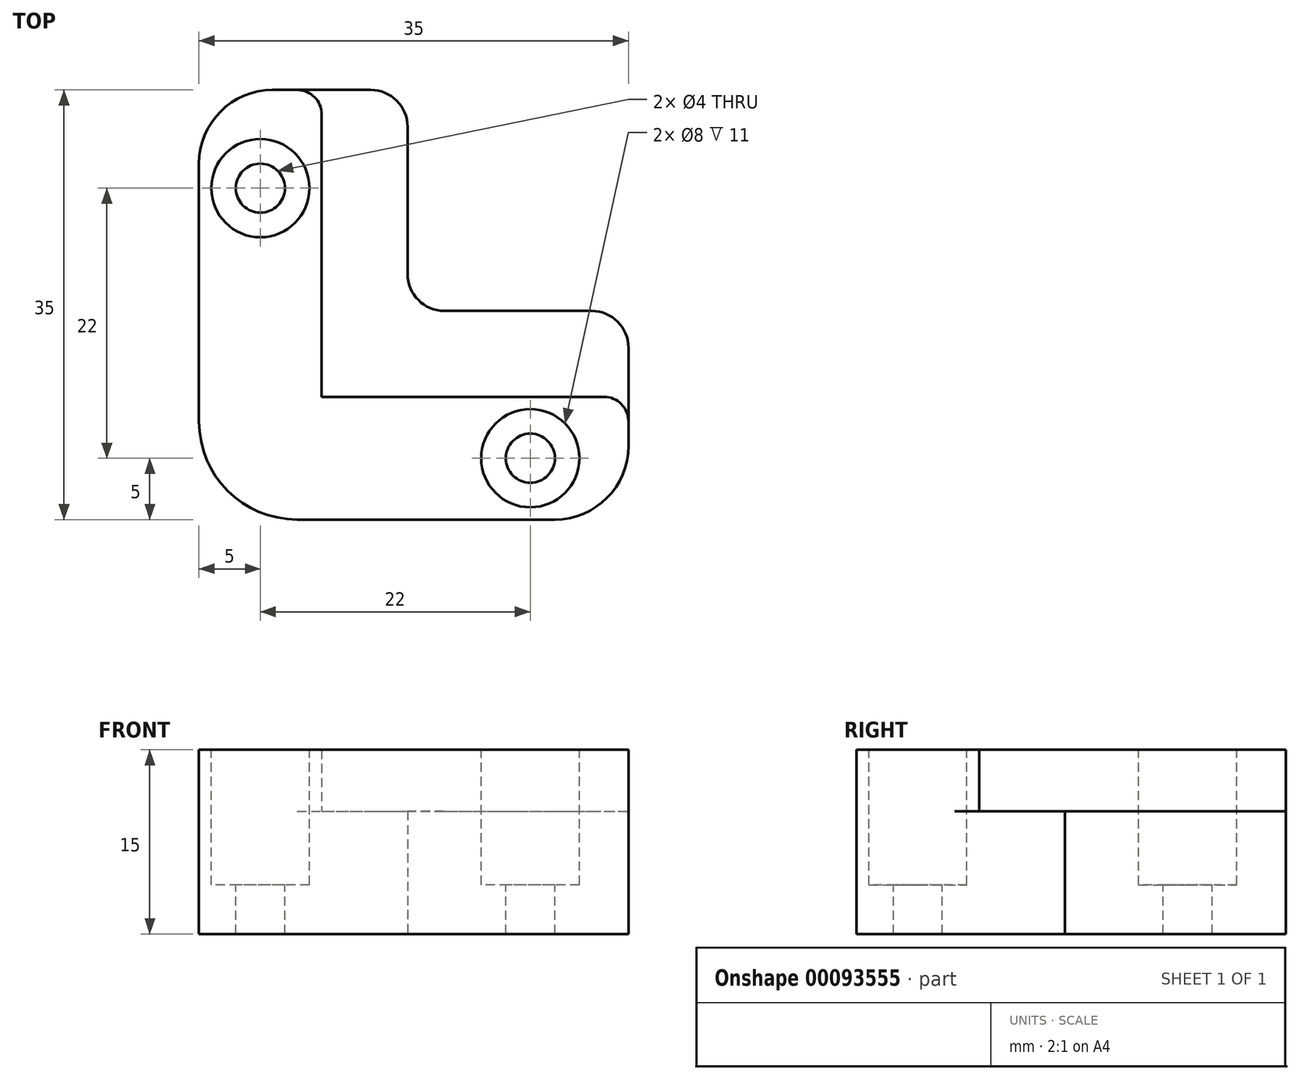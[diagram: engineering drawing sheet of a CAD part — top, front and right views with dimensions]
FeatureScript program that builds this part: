
annotation { "Feature Type Name" : "Feature", "Feature Type Description" : "" }
export const myFeature = defineFeature(function(context is Context, id is Id, definition is map)
    precondition{}
    {
        {
            var Q0;
            Q0=qCreatedBy(makeId("Top.planeOp"),FACE);
            var sketch = newSketch(context, id + "F0", { "sketchPlane" : qUnion([Q0])});
            skLineSegment(sketch, "E0", {"start": v(0, 0) * mm, "end": v(25, 0) * mm});
            skLineSegment(sketch, "E1", {"start": v(25, 0) * mm, "end": v(25, -10) * mm});
            skLineSegment(sketch, "E2", {"start": v(25, -10) * mm, "end": v(-10, -10) * mm});
            skLineSegment(sketch, "E3", {"start": v(-10, -10) * mm, "end": v(-10, 25) * mm});
            skLineSegment(sketch, "E4", {"start": v(-10, 25) * mm, "end": v(0, 25) * mm});
            skLineSegment(sketch, "E5", {"start": v(0, 25) * mm, "end": v(0, 0) * mm});
            skSolve(sketch);
        }
        {
            var Q0;
            Q0 = qSketchRegion(id + "F0", true);
            extrude(context, id + "F1", {"entities" : qUnion([Q0]), "depth" : 15 * mm});
        }
        {
            var Q0;
            Q0=makeQuery(id+"F1.opExtrude","CAP_FACE",FACE,{"disambiguationData":[OSD([sQuery(id+"F0.wireOp",EDGE,"E0"),sQuery(id+"F0.wireOp",EDGE,"E1"),sQuery(id+"F0.wireOp",EDGE,"E2"),sQuery(id+"F0.wireOp",EDGE,"E3"),sQuery(id+"F0.wireOp",EDGE,"E4"),sQuery(id+"F0.wireOp",EDGE,"E5")])],"isStart":true});
            var sketch = newSketch(context, id + "F2", { "sketchPlane" : qUnion([Q0])});
            skLineSegment(sketch, "E6", {"start": v(0, 0) * mm, "end": v(0, -25) * mm});
            skLineSegment(sketch, "E7", {"start": v(0, -25) * mm, "end": v(7, -25) * mm});
            skLineSegment(sketch, "E8", {"start": v(7, -25) * mm, "end": v(7, -7) * mm});
            skLineSegment(sketch, "E9", {"start": v(7, -7) * mm, "end": v(25, -7) * mm});
            skLineSegment(sketch, "E10", {"start": v(25, -7) * mm, "end": v(25, 0) * mm});
            skLineSegment(sketch, "E11", {"start": v(25, 0) * mm, "end": v(0, 0) * mm});
            skSolve(sketch);
        }
        {
            var Q0;
            Q0 = qSketchRegion(id + "F2", true);
            extrude(context, id + "F3", {"entities" : qUnion([Q0]), "operationType" : NewBodyOperationType.ADD, "oppositeDirection" : true, "depth" : 10 * mm});
        }
        {
            var Q0;
            Q0=makeQuery(id+"F1.opExtrude","CAP_FACE",FACE,{"disambiguationData":[OSD([sQuery(id+"F0.wireOp",EDGE,"E0"),sQuery(id+"F0.wireOp",EDGE,"E1"),sQuery(id+"F0.wireOp",EDGE,"E2"),sQuery(id+"F0.wireOp",EDGE,"E3"),sQuery(id+"F0.wireOp",EDGE,"E4"),sQuery(id+"F0.wireOp",EDGE,"E5")])],"isStart":false});
            var sketch = newSketch(context, id + "F4", { "sketchPlane" : qUnion([Q0])});
            skLineSegment(sketch, "E12", {"start": v(25, -5) * mm, "end": v(-10, -5) * mm, "construction": true});
            skLineSegment(sketch, "E13", {"start": v(-5, 25) * mm, "end": v(-5, -10) * mm, "construction": true});
            skCircle(sketch, "E14", {"center": v(17, -5) * mm, "radius": 2 * mm});
            skCircle(sketch, "E15", {"center": v(-5, 17) * mm, "radius": 2 * mm});
            skSolve(sketch);
        }
        {
            var Q0;
            Q0 = qSketchRegion(id + "F4", true);
            extrude(context, id + "F5", {"entities" : qUnion([Q0]), "operationType" : NewBodyOperationType.REMOVE, "oppositeDirection" : true, "depth" : 25 * mm});
        }
        {
            var Q0;
            Q0=makeQuery(id+"F1.opExtrude","CAP_FACE",FACE,{"disambiguationData":[OSD([sQuery(id+"F0.wireOp",EDGE,"E0"),sQuery(id+"F0.wireOp",EDGE,"E1"),sQuery(id+"F0.wireOp",EDGE,"E2"),sQuery(id+"F0.wireOp",EDGE,"E3"),sQuery(id+"F0.wireOp",EDGE,"E4"),sQuery(id+"F0.wireOp",EDGE,"E5")])],"isStart":false});
            var sketch = newSketch(context, id + "F6", { "sketchPlane" : qUnion([Q0])});
            skCircle(sketch, "E16", {"center": v(17, -5) * mm, "radius": 4 * mm});
            skCircle(sketch, "E17", {"center": v(-5, 17) * mm, "radius": 4 * mm});
            skSolve(sketch);
        }
        {
            var Q0;
            Q0 = qSketchRegion(id + "F6", true);
            extrude(context, id + "F7", {"entities" : qUnion([Q0]), "operationType" : NewBodyOperationType.REMOVE, "oppositeDirection" : true, "depth" : 11 * mm});
        }
        {
            var Q0;
            Q0=makeQuery(id+"F1.opExtrude","SWEPT_EDGE",EDGE,{"disambiguationData":[OSD([sQuery(id+"F0.wireOp",EDGE,"E2"),sQuery(id+"F0.wireOp",EDGE,"E3")])]});
            fillet(context, id + "F8", {"entities" : qUnion([Q0]), "radius" : 8 * mm, "tangentPropagation" : true, "allowEdgeOverflow" : false});
        }
        {
            var Q0;
            Q0=makeQuery(id+"F1.opExtrude","SWEPT_EDGE",EDGE,{"disambiguationData":[OSD([sQuery(id+"F0.wireOp",EDGE,"E1"),sQuery(id+"F0.wireOp",EDGE,"E2")])]});
            var Q1;
            Q1=makeQuery(id+"F1.opExtrude","SWEPT_EDGE",EDGE,{"disambiguationData":[OSD([sQuery(id+"F0.wireOp",EDGE,"E3"),sQuery(id+"F0.wireOp",EDGE,"E4")])]});
            fillet(context, id + "F9", {"entities" : qUnion([Q0, Q1]), "radius" : 6 * mm, "tangentPropagation" : true, "allowEdgeOverflow" : false});
        }
        {
            var Q0;
            Q0=makeQuery(id+"F3.opExtrude","SWEPT_EDGE",EDGE,{"disambiguationData":[OSD([sQuery(id+"F2.wireOp",EDGE,"E9"),sQuery(id+"F2.wireOp",EDGE,"E10")])]});
            var Q1;
            Q1=makeQuery(id+"F3.opExtrude","SWEPT_EDGE",EDGE,{"disambiguationData":[OSD([sQuery(id+"F2.wireOp",EDGE,"E8"),sQuery(id+"F2.wireOp",EDGE,"E9")])]});
            var Q2;
            Q2=makeQuery(id+"F3.opExtrude","SWEPT_EDGE",EDGE,{"disambiguationData":[OSD([sQuery(id+"F2.wireOp",EDGE,"E7"),sQuery(id+"F2.wireOp",EDGE,"E8")])]});
            fillet(context, id + "F10", {"entities" : qUnion([Q0, Q1, Q2]), "radius" : 3 * mm, "tangentPropagation" : true, "allowEdgeOverflow" : false});
        }
        {
            var Q0;
            Q0=makeQuery(id+"F1.opExtrude","SWEPT_EDGE",EDGE,{"disambiguationData":[OSD([sQuery(id+"F0.wireOp",EDGE,"E0"),sQuery(id+"F0.wireOp",EDGE,"E1")])]});
            var Q1;
            Q1=makeQuery(id+"F1.opExtrude","SWEPT_EDGE",EDGE,{"disambiguationData":[OSD([sQuery(id+"F0.wireOp",EDGE,"E4"),sQuery(id+"F0.wireOp",EDGE,"E5")])]});
            fillet(context, id + "F11", {"entities" : qUnion([Q0, Q1]), "radius" : 2 * mm, "tangentPropagation" : true, "allowEdgeOverflow" : false});
        }
    });
